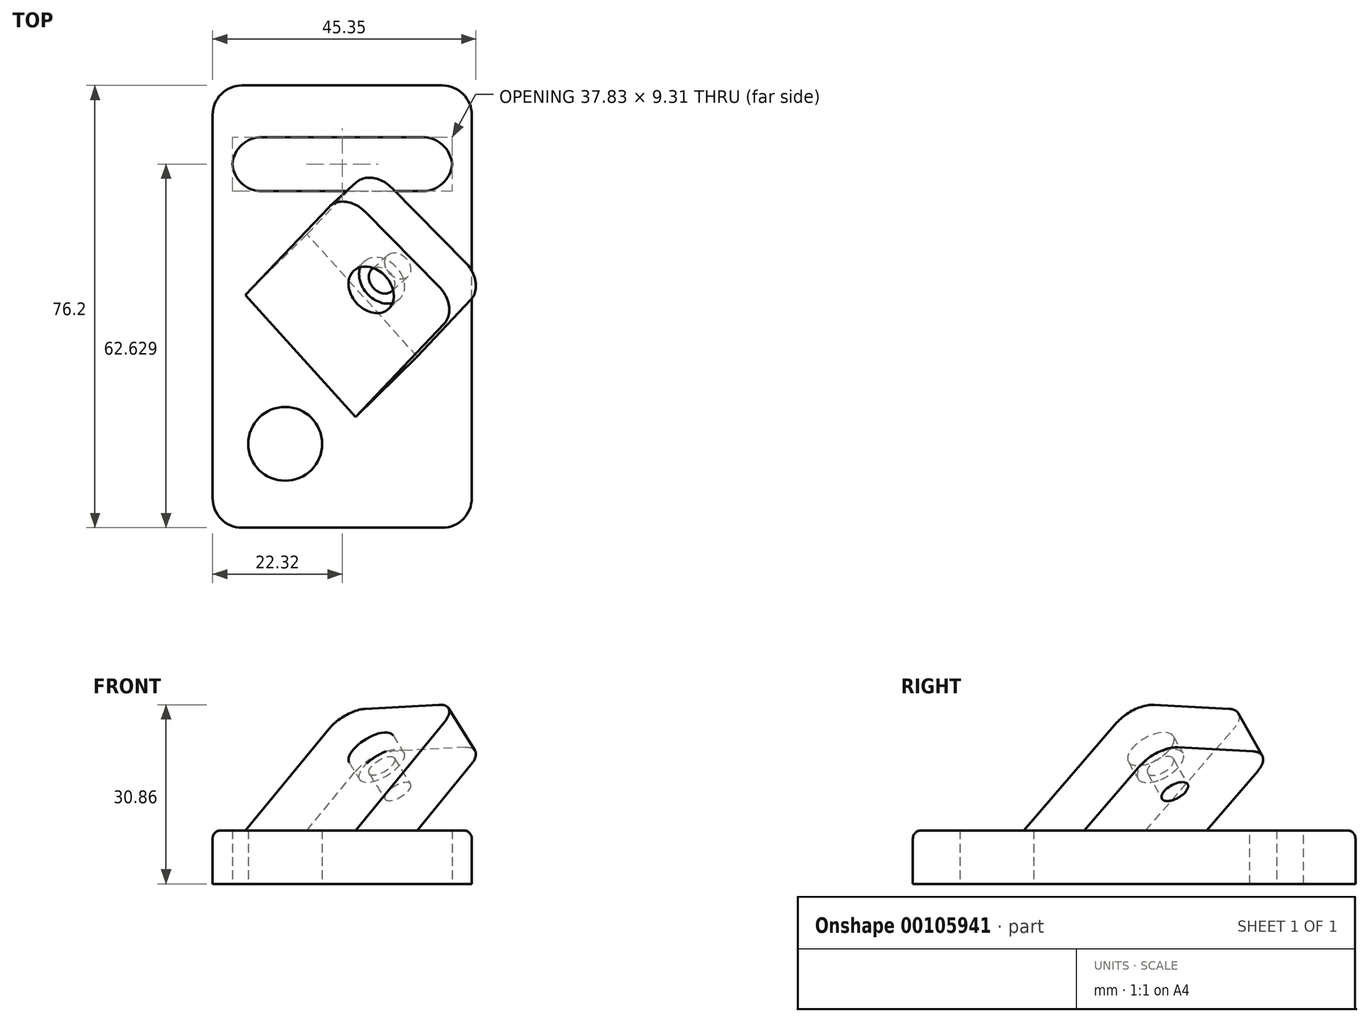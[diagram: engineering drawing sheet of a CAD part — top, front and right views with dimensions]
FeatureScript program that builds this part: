
annotation { "Feature Type Name" : "Feature", "Feature Type Description" : "" }
export const myFeature = defineFeature(function(context is Context, id is Id, definition is map)
    precondition{}
    {
        {
            var Q0;
            Q0=qCreatedBy(makeId("Top.planeOp"),FACE);
            var sketch = newSketch(context, id + "F0", { "sketchPlane" : qUnion([Q0])});
            skLineSegment(sketch, "E0.bottom", {"start": v(22.32, -38.1) * mm, "end": v(-22.32, -38.1) * mm});
            skLineSegment(sketch, "E0.top", {"start": v(22.32, 38.1) * mm, "end": v(-22.32, 38.1) * mm});
            skLineSegment(sketch, "E0.left", {"start": v(22.32, -38.1) * mm, "end": v(22.32, 38.1) * mm});
            skLineSegment(sketch, "E0.right", {"start": v(-22.32, -38.1) * mm, "end": v(-22.32, 38.1) * mm});
            skPoint(sketch, "E0.middle", {"position": v(0, 0) * mm});
            skCircle(sketch, "E1", {"center": v(-9.81, -23.65) * mm, "radius": 6.37 * mm});
            skLineSegment(sketch, "E2", {"start": v(0, 29.18) * mm, "end": v(16.86, 29.18) * mm});
            skLineSegment(sketch, "E3.MirrorCS", {"start": v(0, 29.18) * mm, "end": v(-16.86, 29.18) * mm});
            skLineSegment(sketch, "E4", {"start": v(0, 19.87) * mm, "end": v(16.87, 19.87) * mm});
            skLineSegment(sketch, "E5.MirrorCS", {"start": v(0, 19.87) * mm, "end": v(-16.87, 19.87) * mm});
            skArc(sketch, "E6", {"start": v(-16.86, 29.18) * mm, "mid": v(-19.03, 24.53) * mm, "end": v(-16.87, 19.87) * mm});
            skArc(sketch, "E7.MirrorCS", {"start": v(16.86, 29.18) * mm, "mid": v(19.03, 24.53) * mm, "end": v(16.87, 19.87) * mm});
            skLineSegment(sketch, "E8", {"start": v(0, 0) * mm, "end": v(13.59, 12.07) * mm});
            skSolve(sketch);
        }
        {
            var Q0;
            Q0=makeQuery(id+"F0.imprint","IMPRINT",FACE,{"disambiguationData":[TD([[makeQuery(id+"F0.imprint","IMPRINT",EDGE,{"derivedFrom":sQuery(id+"F0.wireOp",EDGE,"E0.bottom")}),-1.0]])]});
            extrude(context, id + "F1", {"entities" : qUnion([Q0]), "depth" : 9.2 * mm});
        }
        {
            var Q0;
            Q0=makeQuery(id+"F1.opExtrude","SWEPT_EDGE",EDGE,{"disambiguationData":[OSD([sQuery(id+"F0.wireOp",EDGE,"E5.MirrorCS"),sQuery(id+"F0.wireOp",EDGE,"E6")])]});
            var Q1;
            Q1=makeQuery(id+"F1.opExtrude","SWEPT_EDGE",EDGE,{"disambiguationData":[OSD([sQuery(id+"F0.wireOp",EDGE,"E4"),sQuery(id+"F0.wireOp",EDGE,"E7.MirrorCS")])]});
            var Q2;
            Q2=makeQuery(id+"F1.opExtrude","SWEPT_EDGE",EDGE,{"disambiguationData":[OSD([sQuery(id+"F0.wireOp",EDGE,"E3.MirrorCS"),sQuery(id+"F0.wireOp",EDGE,"E6")])]});
            var Q3;
            Q3=makeQuery(id+"F1.opExtrude","SWEPT_EDGE",EDGE,{"disambiguationData":[OSD([sQuery(id+"F0.wireOp",EDGE,"E2"),sQuery(id+"F0.wireOp",EDGE,"E7.MirrorCS")])]});
            fillet(context, id + "F2", {"entities" : qUnion([Q0, Q1, Q2, Q3]), "radius" : 5.08 * mm, "tangentPropagation" : true, "allowEdgeOverflow" : false});
        }
        {
            var Q0;
            Q0=makeQuery(id+"F1.opExtrude","SWEPT_EDGE",EDGE,{"disambiguationData":[OSD([sQuery(id+"F0.wireOp",EDGE,"E0.bottom"),sQuery(id+"F0.wireOp",EDGE,"E0.left")])]});
            var Q1;
            Q1=makeQuery(id+"F1.opExtrude","SWEPT_EDGE",EDGE,{"disambiguationData":[OSD([sQuery(id+"F0.wireOp",EDGE,"E0.top"),sQuery(id+"F0.wireOp",EDGE,"E0.left")])]});
            var Q2;
            Q2=makeQuery(id+"F1.opExtrude","SWEPT_EDGE",EDGE,{"disambiguationData":[OSD([sQuery(id+"F0.wireOp",EDGE,"E0.top"),sQuery(id+"F0.wireOp",EDGE,"E0.right")])]});
            var Q3;
            Q3=makeQuery(id+"F1.opExtrude","SWEPT_EDGE",EDGE,{"disambiguationData":[OSD([sQuery(id+"F0.wireOp",EDGE,"E0.bottom"),sQuery(id+"F0.wireOp",EDGE,"E0.right")])]});
            fillet(context, id + "F3", {"entities" : qUnion([Q0, Q1, Q2, Q3]), "radius" : 5.08 * mm, "tangentPropagation" : true, "allowEdgeOverflow" : false});
        }
        {
            var Q0;
            Q0=makeQuery(id+"F1.opExtrude","CAP_EDGE",EDGE,{"disambiguationData":[OSD([sQuery(id+"F0.wireOp",EDGE,"E0.right")])],"isStart":false});
            fillet(context, id + "F4", {"entities" : qUnion([Q0]), "radius" : 1.4 * mm, "tangentPropagation" : true, "allowEdgeOverflow" : false});
        }
        {
            var Q0;
            Q0=makeQuery(id+"F1.opExtrude","CAP_FACE",FACE,{"disambiguationData":[OSD([sQuery(id+"F0.wireOp",EDGE,"E0.bottom"),sQuery(id+"F0.wireOp",EDGE,"E0.top"),sQuery(id+"F0.wireOp",EDGE,"E0.left"),sQuery(id+"F0.wireOp",EDGE,"E0.right"),sQuery(id+"F0.wireOp",EDGE,"E1"),sQuery(id+"F0.wireOp",EDGE,"E2"),sQuery(id+"F0.wireOp",EDGE,"E3.MirrorCS"),sQuery(id+"F0.wireOp",EDGE,"E4"),sQuery(id+"F0.wireOp",EDGE,"E5.MirrorCS"),sQuery(id+"F0.wireOp",EDGE,"E6"),sQuery(id+"F0.wireOp",EDGE,"E7.MirrorCS")])],"isStart":false});
            var sketch = newSketch(context, id + "F5", { "sketchPlane" : qUnion([Q0])});
            skLineSegment(sketch, "E9", {"start": v(10.06, -9.56) * mm, "end": v(0, 0) * mm});
            skLineSegment(sketch, "E10.MirrorCS", {"start": v(-10.06, 9.56) * mm, "end": v(0, 0) * mm});
            skLineSegment(sketch, "E11", {"start": v(-10.06, 9.56) * mm, "end": v(10.06, -9.56) * mm});
            skSolve(sketch);
        }
        {
            var Q0;
            Q0=sQuery(id+"F5.wireOp",EDGE,"E11");
            cPlane(context, id + "F6", {"entities" : qUnion([Q0]), "cplaneType" : CPlaneType.LINE_ANGLE, "offset" : 25.4 * mm, "angle" : 0 * degree, "width" : 152.4 * mm, "height" : 152.4 * mm});
        }
        {
            var Q0;
            Q0=qCreatedBy(id+"F6.planeOp",FACE);
            var sketch = newSketch(context, id + "F7", { "sketchPlane" : qUnion([Q0])});
            skLineSegment(sketch, "E12", {"start": v(15.04, 20.46) * mm, "end": v(-14.63, 20.46) * mm});
            skSolve(sketch);
        }
        {
            var Q0;
            Q0=sQuery(id+"F7.wireOp",EDGE,"E12");
            cPlane(context, id + "F8", {"entities" : qUnion([Q0]), "cplaneType" : CPlaneType.LINE_ANGLE, "offset" : 25.4 * mm, "angle" : 220 * degree, "width" : 152.4 * mm, "height" : 152.4 * mm});
        }
        {
            var Q0;
            Q0=qCreatedBy(id+"F8.planeOp",FACE);
            var sketch = newSketch(context, id + "F9", { "sketchPlane" : qUnion([Q0])});
            skLineSegment(sketch, "E13", {"start": v(10.24, 12.51) * mm, "end": v(-13.11, -3.41) * mm});
            skLineSegment(sketch, "E14", {"start": v(-13.11, -3.41) * mm, "end": v(-18.5, 4.5) * mm});
            skLineSegment(sketch, "E15", {"start": v(-18.5, 4.5) * mm, "end": v(4.85, 20.43) * mm});
            skLineSegment(sketch, "E16", {"start": v(4.85, 20.43) * mm, "end": v(10.24, 12.51) * mm});
            skSolve(sketch);
        }
        {
            var Q0;
            Q0 = qSketchRegion(id + "F9", true);
            extrude(context, id + "F10", {"entities" : qUnion([Q0]), "operationType" : NewBodyOperationType.ADD, "depth" : 34.78 * mm, "symmetric" : true});
        }
        {
            var Q0;
            Q0=makeQuery(id+"F10.opExtrude","SWEPT_FACE",FACE,{"disambiguationData":[OSD([sQuery(id+"F9.wireOp",EDGE,"E15")])]});
            var sketch = newSketch(context, id + "F11", { "sketchPlane" : qUnion([Q0])});
            skCircle(sketch, "E17", {"center": v(13.39, 13.9) * mm, "radius": 4.53 * mm});
            skSolve(sketch);
        }
        {
            var Q0;
            Q0=makeQuery(id+"F10.opExtrude","CAP_EDGE",EDGE,{"disambiguationData":[OSD([sQuery(id+"F9.wireOp",EDGE,"E16")])],"isStart":true});
            var Q1;
            Q1=makeQuery(id+"F10.opExtrude","CAP_EDGE",EDGE,{"disambiguationData":[OSD([sQuery(id+"F9.wireOp",EDGE,"E14")])],"isStart":true});
            fillet(context, id + "F12", {"entities" : qUnion([Q0, Q1]), "radius" : 5.08 * mm, "tangentPropagation" : true, "allowEdgeOverflow" : false});
        }
        {
            var Q0;
            Q0=sQuery(id+"F11.wireOp",VERTEX,"E17.center");
            var Q1;
            Q1=makeQuery(id+"F1.opExtrude","SWEPT_BODY",BODY,{"disambiguationData":[OSD([sQuery(id+"F0.wireOp",EDGE,"E0.bottom"),sQuery(id+"F0.wireOp",EDGE,"E0.top"),sQuery(id+"F0.wireOp",EDGE,"E0.left"),sQuery(id+"F0.wireOp",EDGE,"E0.right"),sQuery(id+"F0.wireOp",EDGE,"E1"),sQuery(id+"F0.wireOp",EDGE,"E2"),sQuery(id+"F0.wireOp",EDGE,"E3.MirrorCS"),sQuery(id+"F0.wireOp",EDGE,"E4"),sQuery(id+"F0.wireOp",EDGE,"E5.MirrorCS"),sQuery(id+"F0.wireOp",EDGE,"E6"),sQuery(id+"F0.wireOp",EDGE,"E7.MirrorCS")])]});
            hole(context, id + "F13", {"style" : HoleStyle.C_BORE, "endStyle" : HoleEndStyle.BLIND, "holeDiameter" : 5.08 * mm, "cBoreDiameter" : 8.9 * mm, "cBoreDepth" : 3.8 * mm, "holeDepth" : 12.7 * mm, "locations" : qUnion([Q0]), "scope" : qUnion([Q1])});
        }
    });
